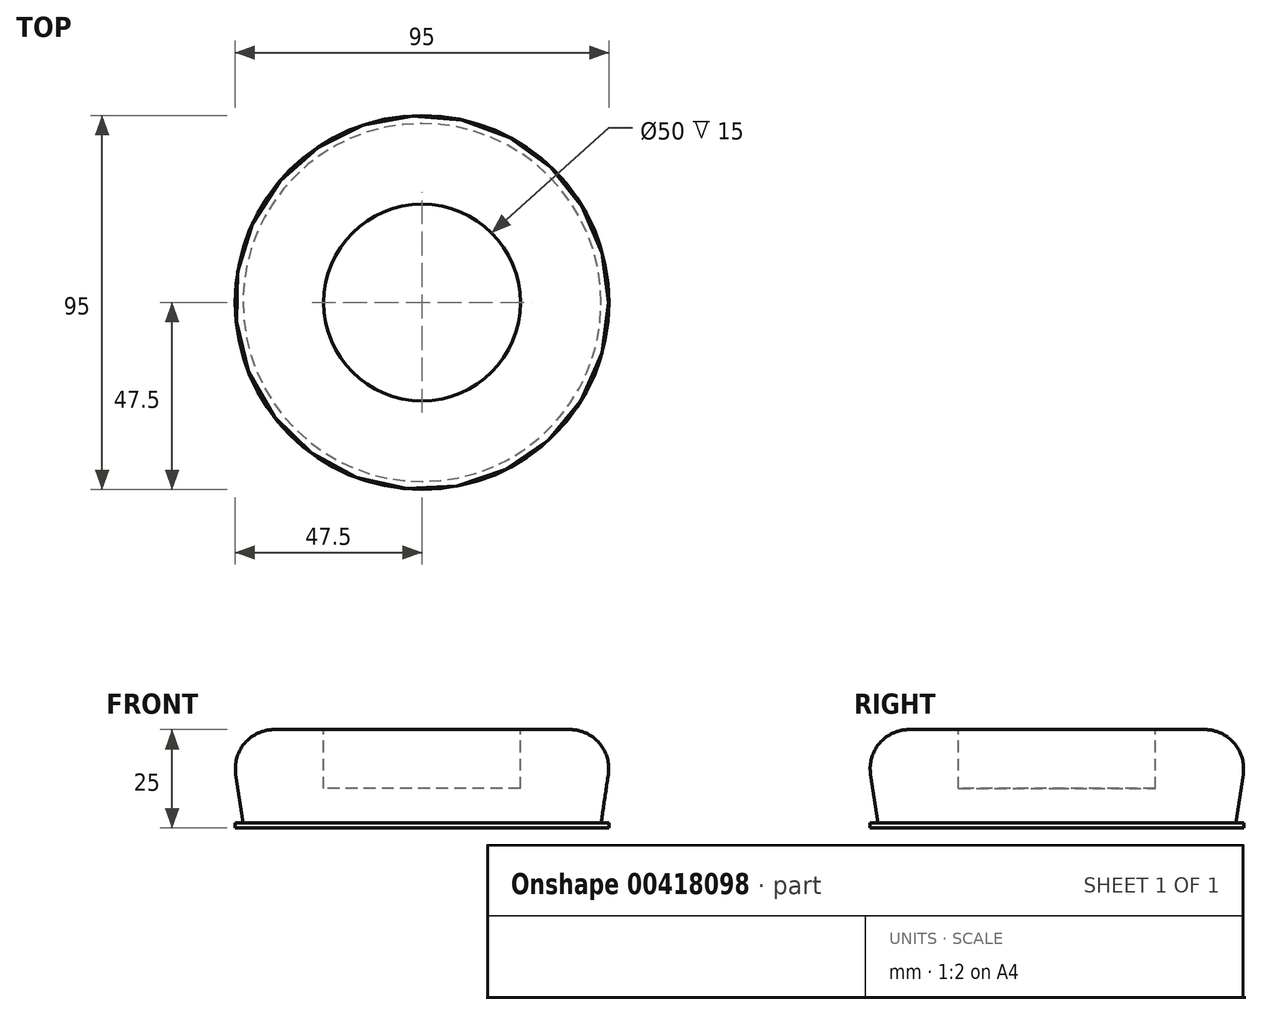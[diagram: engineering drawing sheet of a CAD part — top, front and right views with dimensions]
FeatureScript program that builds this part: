
annotation { "Feature Type Name" : "Feature", "Feature Type Description" : "" }
export const myFeature = defineFeature(function(context is Context, id is Id, definition is map)
    precondition{}
    {
        {
            var Q0;
            Q0=qCreatedBy(makeId("Top.planeOp"),FACE);
            var sketch = newSketch(context, id + "F0", { "sketchPlane" : qUnion([Q0])});
            skCircle(sketch, "E0", {"center": v(0, 0) * mm, "radius": 47.5 * mm});
            skSolve(sketch);
        }
        {
            var Q0;
            Q0=makeQuery(id+"F0.imprint","IMPRINT",FACE,{"disambiguationData":[TD([[makeQuery(id+"F0.imprint","IMPRINT",EDGE,{"derivedFrom":sQuery(id+"F0.wireOp",EDGE,"E0")}),1.0]])]});
            extrude(context, id + "F1", {"entities" : qUnion([Q0]), "depth" : 25 * mm});
        }
        {
            var Q0;
            Q0=makeQuery(id+"F1.opExtrude","CAP_FACE",FACE,{"disambiguationData":[OSD([sQuery(id+"F0.wireOp",EDGE,"E0")])],"isStart":false});
            var sketch = newSketch(context, id + "F2", { "sketchPlane" : qUnion([Q0])});
            skCircle(sketch, "E1", {"center": v(0, 0) * mm, "radius": 25 * mm});
            skSolve(sketch);
        }
        {
            var Q0;
            Q0=makeQuery(id+"F2.imprint","IMPRINT",FACE,{"disambiguationData":[TD([[makeQuery(id+"F2.imprint","IMPRINT",EDGE,{"derivedFrom":sQuery(id+"F2.wireOp",EDGE,"E1")}),1.0]])]});
            extrude(context, id + "F3", {"entities" : qUnion([Q0]), "operationType" : NewBodyOperationType.REMOVE, "oppositeDirection" : true, "depth" : 15 * mm});
        }
        {
            var Q0;
            Q0=makeQuery(id+"F1.opExtrude","CAP_EDGE",EDGE,{"disambiguationData":[OSD([sQuery(id+"F0.wireOp",EDGE,"E0")])],"isStart":false});
            var Q1;
            Q1=makeQuery(id+"F3.boolean.opBoolean","COPY",EDGE,{"derivedFrom":makeQuery(id+"F3.opExtrude","CAP_EDGE",EDGE,{"disambiguationData":[OSD([sQuery(id+"F2.wireOp",EDGE,"E1")])],"isStart":true})});
            fillet(context, id + "F4", {"entities" : qUnion([Q0, Q1]), "radius" : 10 * mm, "tangentPropagation" : true, "allowEdgeOverflow" : false});
        }
        {
            var Q0;
            Q0=qCreatedBy(makeId("Front.planeOp"),FACE);
            var sketch = newSketch(context, id + "F5", { "sketchPlane" : qUnion([Q0])});
            skLineSegment(sketch, "E2", {"start": v(-47.5, 0) * mm, "end": v(-47.5, 1.3) * mm});
            skLineSegment(sketch, "E3", {"start": v(-47.5, 1.3) * mm, "end": v(-45.5, 1.3) * mm});
            skArc(sketch, "E4", {"start": v(-37.4, 25.05) * mm, "mid": v(-45, 21.6) * mm, "end": v(-47.32, 13.59) * mm});
            skLineSegment(sketch, "E5", {"start": v(-47.32, 13.59) * mm, "end": v(-45.5, 1.3) * mm});
            skLineSegment(sketch, "E6", {"start": v(-37.4, 25.05) * mm, "end": v(-37.4, 26.94) * mm});
            skLineSegment(sketch, "E7", {"start": v(-37.4, 26.94) * mm, "end": v(-49.5, 21.7) * mm});
            skLineSegment(sketch, "E8", {"start": v(-49.5, 21.7) * mm, "end": v(-50.88, -0.32) * mm});
            skLineSegment(sketch, "E9", {"start": v(-50.88, -0.32) * mm, "end": v(-47.5, 0) * mm});
            skLineSegment(sketch, "E10", {"start": v(0, 0) * mm, "end": v(0, 34.9) * mm, "construction": true});
            skSolve(sketch);
        }
        {
            var Q0;
            Q0=makeQuery(id+"F5.imprint","IMPRINT",FACE,{"disambiguationData":[TD([[makeQuery(id+"F5.imprint","IMPRINT",EDGE,{"derivedFrom":sQuery(id+"F5.wireOp",EDGE,"E2")}),1.0]])]});
            var Q1;
            Q1=sQuery(id+"F5.wireOp",EDGE,"E10");
            revolve(context, id + "F6", {"operationType" : NewBodyOperationType.REMOVE, "entities" : qUnion([Q0]), "axis" : qUnion([Q1]), "revolveType" : RevolveType.FULL, "oppositeDirection" : true});
        }
    });
